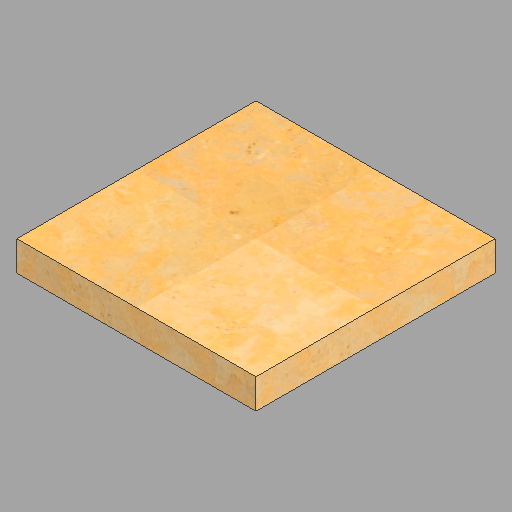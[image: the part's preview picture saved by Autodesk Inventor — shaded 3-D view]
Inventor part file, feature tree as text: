
AUTODESK INVENTOR PART (.ipt)
format: ipt  version: 2023 (Build 270158030, 158C)  size: 264,704 bytes
history: native  units: in
note: dims shown in document units (in); Inventor stores cm internally (conversion verified against a paired STEP export)
features: other x1, extrude x1, sketch x1
ambient origin geometry x8: Origin, YZ Plane, XZ Plane, XY Plane, X Axis, Y Axis, Z Axis, Center Point
bodies: Solid1 (feature_tree)
feature tree (3):
  other  "16x16x2 - 53"
  extrude  "Extrusion1"  Depth=16.0in
  sketch  "Sketch1"  dims[d0=16.0in d1=16.0in d2=2.0in d3=0.0in]
